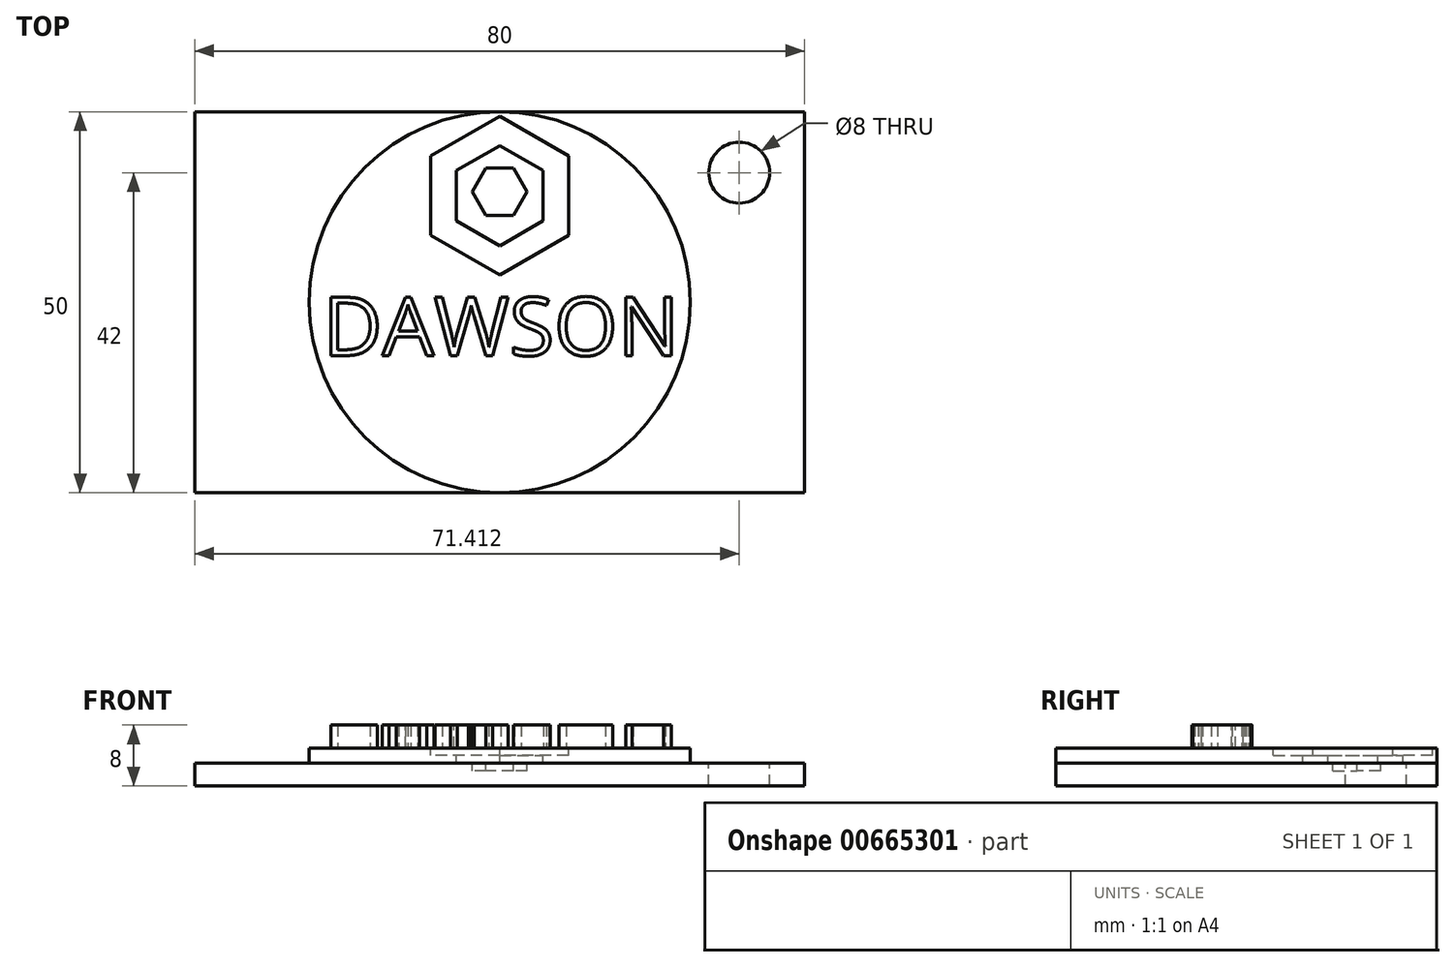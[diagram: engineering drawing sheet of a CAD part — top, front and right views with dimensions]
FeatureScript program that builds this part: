
annotation { "Feature Type Name" : "Feature", "Feature Type Description" : "" }
export const myFeature = defineFeature(function(context is Context, id is Id, definition is map)
    precondition{}
    {
        {
            var Q0;
            Q0=qCreatedBy(makeId("Top.planeOp"),FACE);
            var sketch = newSketch(context, id + "F0", { "sketchPlane" : qUnion([Q0])});
            skLineSegment(sketch, "E0.bottom", {"start": v(-40, 25) * mm, "end": v(40, 25) * mm});
            skLineSegment(sketch, "E0.top", {"start": v(-40, -25) * mm, "end": v(40, -25) * mm});
            skLineSegment(sketch, "E0.left", {"start": v(-40, 25) * mm, "end": v(-40, -25) * mm});
            skLineSegment(sketch, "E0.right", {"start": v(40, 25) * mm, "end": v(40, -25) * mm});
            skPoint(sketch, "E0.middle", {"position": v(0, 0) * mm});
            skSolve(sketch);
        }
        {
            var Q0;
            Q0=makeQuery(id+"F0.imprint","IMPRINT",FACE,{"disambiguationData":[TD([[makeQuery(id+"F0.imprint","IMPRINT",EDGE,{"derivedFrom":sQuery(id+"F0.wireOp",EDGE,"E0.bottom")}),-1.0]])]});
            var sketch = newSketch(context, id + "F1", { "sketchPlane" : qUnion([Q0])});
            skSolve(sketch);
        }
        {
            var Q0;
            Q0=makeQuery(id+"F1.imprint","IMPRINT",FACE,{"disambiguationData":[TD([[makeQuery(id+"F1.imprint","IMPRINT",EDGE,{"derivedFrom":makeQuery(id+"F0.imprint","IMPRINT",EDGE,{"derivedFrom":sQuery(id+"F0.wireOp",EDGE,"E0.bottom")})}),-1.0]])]});
            extrude(context, id + "F2", {"entities" : qUnion([Q0]), "depth" : 3 * mm, "offsetDistance" : 25 * mm});
        }
        {
            var Q0;
            Q0=makeQuery(id+"F2.opExtrude","CAP_FACE",FACE,{"disambiguationData":[OSD([sQuery(id+"F0.wireOp",EDGE,"E0.bottom"),sQuery(id+"F0.wireOp",EDGE,"E0.top"),sQuery(id+"F0.wireOp",EDGE,"E0.left"),sQuery(id+"F0.wireOp",EDGE,"E0.right")])],"isStart":false});
            var sketch = newSketch(context, id + "F3", { "sketchPlane" : qUnion([Q0])});
            skCircle(sketch, "E1", {"center": v(0, 0) * mm, "radius": 25 * mm});
            skSolve(sketch);
        }
        {
            var Q0;
            {var subQ0=sQuery(id+"F3.wireOp",EDGE,"E1");var subQ1=makeQuery(id+"F3.imprint","INTERSECT",VERTEX,{"derivedFrom":[makeQuery(id+"F2.opExtrude","CAP_EDGE",EDGE,{"disambiguationData":[OSD([sQuery(id+"F0.wireOp",EDGE,"E0.bottom")])],"isStart":false}),subQ0]});Q0=makeQuery(id+"F3.imprint","IMPRINT",FACE,{"disambiguationData":[TD([[makeQuery(id+"F3.imprint","IMPRINT",EDGE,{"disambiguationData":[TD([[subQ1,-1.0]])],"derivedFrom":subQ0}),1.0]])]});}
            extrude(context, id + "F4", {"entities" : qUnion([Q0]), "operationType" : NewBodyOperationType.ADD, "depth" : 2 * mm, "offsetDistance" : 25 * mm});
        }
        {
            var Q0;
            Q0=makeQuery(id+"F4.opExtrude","CAP_FACE",FACE,{"disambiguationData":[OSD([sQuery(id+"F3.wireOp",EDGE,"E1")])],"isStart":false});
            var sketch = newSketch(context, id + "F5", { "sketchPlane" : qUnion([Q0])});
            skCircle(sketch, "E2", {"center": v(31.41, 17) * mm, "radius": 4 * mm});
            skSolve(sketch);
        }
        {
            var Q0;
            Q0=makeQuery(id+"F5.imprint","IMPRINT",FACE,{"disambiguationData":[TD([[makeQuery(id+"F5.imprint","IMPRINT",EDGE,{"derivedFrom":sQuery(id+"F5.wireOp",EDGE,"E2")}),1.0]])]});
            extrude(context, id + "F6", {"entities" : qUnion([Q0]), "operationType" : NewBodyOperationType.REMOVE, "oppositeDirection" : true, "depth" : 3 * mm, "offsetDistance" : 25 * mm});
        }
        {
            var Q0;
            Q0=makeQuery(id+"F5.imprint","IMPRINT",FACE,{"disambiguationData":[TD([[makeQuery(id+"F5.imprint","IMPRINT",EDGE,{"derivedFrom":sQuery(id+"F5.wireOp",EDGE,"E2")}),1.0]])]});
            var Q1;
            Q1=makeQuery(id+"F6.boolean.opBoolean","COPY",FACE,{"derivedFrom":makeQuery(id+"F6.opExtrude","CAP_FACE",FACE,{"disambiguationData":[OSD([sQuery(id+"F5.wireOp",EDGE,"E2")])],"isStart":false})});
            extrude(context, id + "F7", {"entities" : qUnion([Q0, Q1]), "operationType" : NewBodyOperationType.REMOVE, "oppositeDirection" : true, "depth" : 3 * mm, "offsetDistance" : 25 * mm});
        }
        {
            var Q0;
            Q0=makeQuery(id+"F4.opExtrude","CAP_FACE",FACE,{"disambiguationData":[OSD([sQuery(id+"F3.wireOp",EDGE,"E1")])],"isStart":false});
            var sketch = newSketch(context, id + "F8", { "sketchPlane" : qUnion([Q0])});
            skText(sketch, "E3", { "text": "DAWSON\n", "fontName": "OpenSans-Regular.ttf"});
            const initialGuessF8  = {"E3": [-0.0232, -0.007, 1, 0, 0.0077]};
            skSetInitialGuess(sketch, initialGuessF8);
            skSolve(sketch);
        }
        {
            var Q0;
            Q0 = qSketchRegion(id + "F8", true);
            extrude(context, id + "F9", {"entities" : qUnion([Q0]), "operationType" : NewBodyOperationType.ADD, "depth" : 3 * mm, "offsetDistance" : 25 * mm});
        }
        {
            var Q0;
            {var subQ0=sQuery(id+"F3.wireOp",EDGE,"E1");Q0=makeQuery(id+"F9.boolean.opBoolean","SPLIT",FACE,{"disambiguationData":[TD([makeQuery(id+"F4.opExtrude","SWEPT_FACE",FACE,{"disambiguationData":[OSD([subQ0])]})])],"derivedFrom":makeQuery(id+"F4.opExtrude","CAP_FACE",FACE,{"disambiguationData":[OSD([subQ0])],"isStart":false})});}
            var sketch = newSketch(context, id + "F10", { "sketchPlane" : qUnion([Q0])});
            skCircle(sketch, "E4.cCircle", {"center": v(0, 13.98) * mm, "radius": 9.03 * mm, "construction": true});
            skLineSegment(sketch, "E4.0", {"start": v(-9.03, 8.77) * mm, "end": v(-9.03, 19.2) * mm});
            skLineSegment(sketch, "E4.1", {"start": v(-9.03, 19.2) * mm, "end": v(0, 24.4) * mm});
            skLineSegment(sketch, "E4.2", {"start": v(0, 24.4) * mm, "end": v(9.03, 19.2) * mm});
            skLineSegment(sketch, "E4.3", {"start": v(9.03, 19.2) * mm, "end": v(9.03, 8.77) * mm});
            skLineSegment(sketch, "E4.4", {"start": v(9.03, 8.77) * mm, "end": v(0, 3.56) * mm});
            skLineSegment(sketch, "E4.5", {"start": v(0, 3.56) * mm, "end": v(-9.03, 8.77) * mm});
            skPoint(sketch, "E4.0.midPoint", {"position": v(-9.03, 13.98) * mm});
            skSolve(sketch);
        }
        {
            var Q0;
            Q0=makeQuery(id+"F10.imprint","IMPRINT",FACE,{"disambiguationData":[TD([[makeQuery(id+"F10.imprint","IMPRINT",EDGE,{"derivedFrom":sQuery(id+"F10.wireOp",EDGE,"E4.0")}),-1.0]])]});
            extrude(context, id + "F11", {"entities" : qUnion([Q0]), "operationType" : NewBodyOperationType.REMOVE, "oppositeDirection" : true, "depth" : 1 * mm, "offsetDistance" : 25 * mm});
        }
        {
            var Q0;
            Q0=makeQuery(id+"F11.boolean.opBoolean","COPY",FACE,{"derivedFrom":makeQuery(id+"F11.opExtrude","CAP_FACE",FACE,{"disambiguationData":[OSD([sQuery(id+"F10.wireOp",EDGE,"E4.0"),sQuery(id+"F10.wireOp",EDGE,"E4.1"),sQuery(id+"F10.wireOp",EDGE,"E4.2"),sQuery(id+"F10.wireOp",EDGE,"E4.3"),sQuery(id+"F10.wireOp",EDGE,"E4.4"),sQuery(id+"F10.wireOp",EDGE,"E4.5")])],"isStart":false})});
            var sketch = newSketch(context, id + "F12", { "sketchPlane" : qUnion([Q0])});
            skCircle(sketch, "E5.cCircle", {"center": v(0, 13.98) * mm, "radius": 5.7 * mm, "construction": true});
            skLineSegment(sketch, "E5.0", {"start": v(-5.7, 10.69) * mm, "end": v(-5.7, 17.27) * mm});
            skLineSegment(sketch, "E5.1", {"start": v(-5.7, 17.27) * mm, "end": v(0, 20.57) * mm});
            skLineSegment(sketch, "E5.2", {"start": v(0, 20.57) * mm, "end": v(5.7, 17.27) * mm});
            skLineSegment(sketch, "E5.3", {"start": v(5.7, 17.27) * mm, "end": v(5.7, 10.69) * mm});
            skLineSegment(sketch, "E5.4", {"start": v(5.7, 10.69) * mm, "end": v(0, 7.4) * mm});
            skLineSegment(sketch, "E5.5", {"start": v(0, 7.4) * mm, "end": v(-5.7, 10.69) * mm});
            skPoint(sketch, "E5.0.midPoint", {"position": v(-5.7, 13.98) * mm});
            skSolve(sketch);
        }
        {
            var Q0;
            Q0 = qSketchRegion(id + "F12", true);
            extrude(context, id + "F13", {"entities" : qUnion([Q0]), "operationType" : NewBodyOperationType.REMOVE, "oppositeDirection" : true, "depth" : 1 * mm, "offsetDistance" : 25 * mm});
        }
        {
            var Q0;
            Q0=makeQuery(id+"F13.boolean.opBoolean","COPY",FACE,{"derivedFrom":makeQuery(id+"F13.opExtrude","CAP_FACE",FACE,{"disambiguationData":[OSD([sQuery(id+"F12.wireOp",EDGE,"E5.0"),sQuery(id+"F12.wireOp",EDGE,"E5.1"),sQuery(id+"F12.wireOp",EDGE,"E5.2"),sQuery(id+"F12.wireOp",EDGE,"E5.3"),sQuery(id+"F12.wireOp",EDGE,"E5.4"),sQuery(id+"F12.wireOp",EDGE,"E5.5")])],"isStart":false})});
            var sketch = newSketch(context, id + "F14", { "sketchPlane" : qUnion([Q0])});
            skCircle(sketch, "E6.cCircle", {"center": v(0, 14.5) * mm, "radius": 3.13 * mm, "construction": true});
            skLineSegment(sketch, "E6.0", {"start": v(-1.8, 11.38) * mm, "end": v(-3.61, 14.5) * mm});
            skLineSegment(sketch, "E6.1", {"start": v(-3.61, 14.5) * mm, "end": v(-1.8, 17.63) * mm});
            skLineSegment(sketch, "E6.2", {"start": v(-1.8, 17.63) * mm, "end": v(1.8, 17.63) * mm});
            skLineSegment(sketch, "E6.3", {"start": v(1.8, 17.63) * mm, "end": v(3.61, 14.5) * mm});
            skLineSegment(sketch, "E6.4", {"start": v(3.61, 14.5) * mm, "end": v(1.8, 11.38) * mm});
            skLineSegment(sketch, "E6.5", {"start": v(1.8, 11.38) * mm, "end": v(-1.8, 11.38) * mm});
            skPoint(sketch, "E6.0.midPoint", {"position": v(-2.7, 12.94) * mm});
            skSolve(sketch);
        }
        {
            var Q0;
            Q0=makeQuery(id+"F14.imprint","IMPRINT",FACE,{"disambiguationData":[TD([[makeQuery(id+"F14.imprint","IMPRINT",EDGE,{"derivedFrom":sQuery(id+"F14.wireOp",EDGE,"E6.0")}),-1.0]])]});
            extrude(context, id + "F15", {"entities" : qUnion([Q0]), "operationType" : NewBodyOperationType.REMOVE, "oppositeDirection" : true, "depth" : 1 * mm, "offsetDistance" : 25 * mm});
        }
    });
